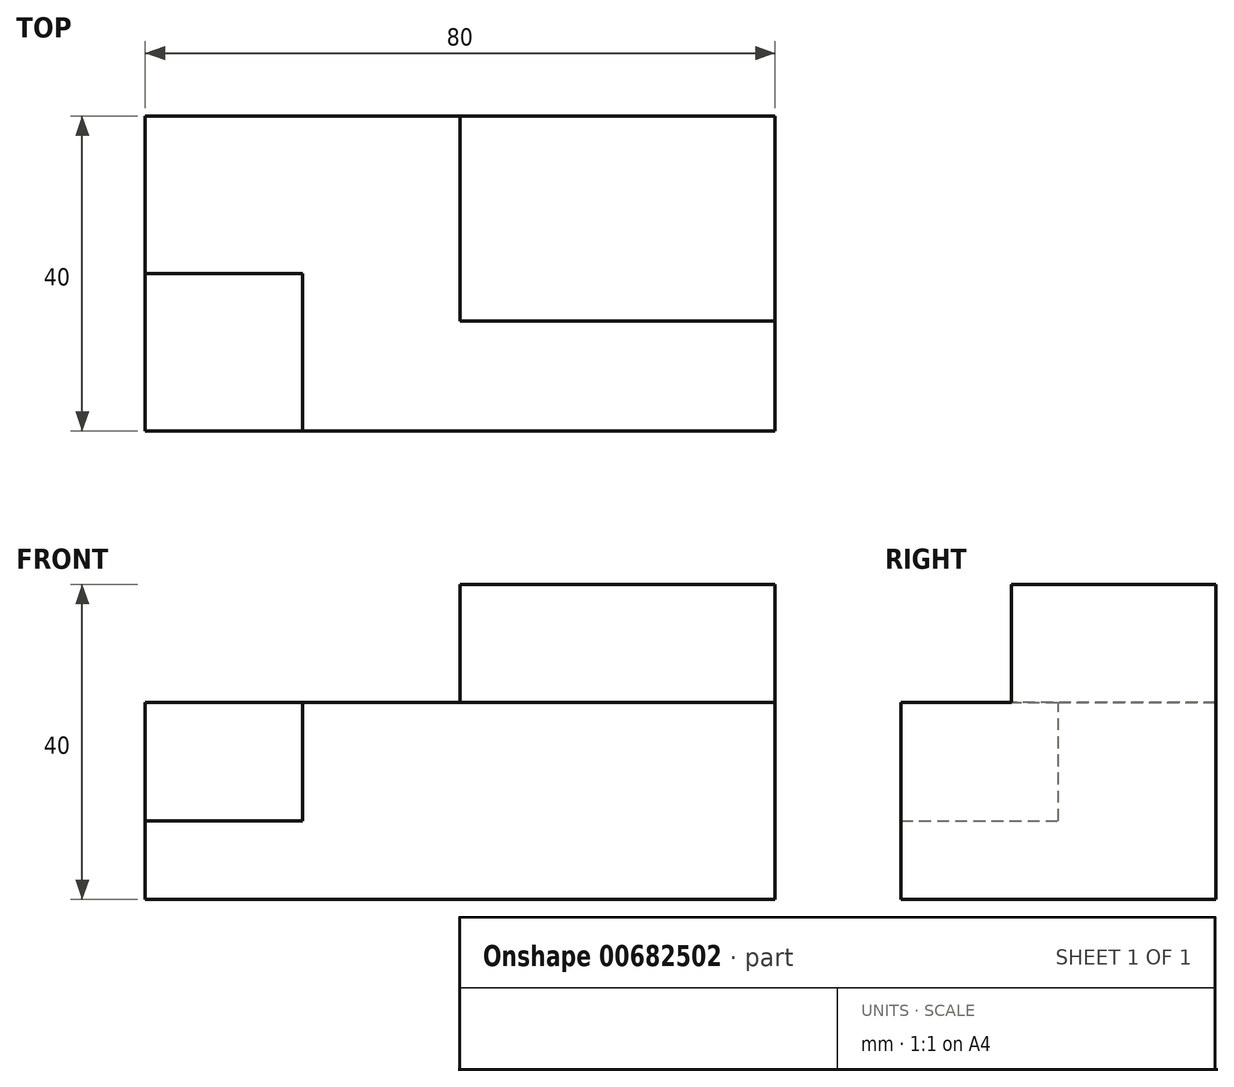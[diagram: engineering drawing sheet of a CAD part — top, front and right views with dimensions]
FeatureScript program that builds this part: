
annotation { "Feature Type Name" : "Feature", "Feature Type Description" : "" }
export const myFeature = defineFeature(function(context is Context, id is Id, definition is map)
    precondition{}
    {
        {
            var Q0;
            Q0=qCreatedBy(makeId("Top.planeOp"),FACE);
            var sketch = newSketch(context, id + "F0", { "sketchPlane" : qUnion([Q0])});
            skLineSegment(sketch, "E0.bottom", {"start": v(0, 0) * mm, "end": v(80, 0) * mm});
            skLineSegment(sketch, "E0.top", {"start": v(0, 40) * mm, "end": v(80, 40) * mm});
            skLineSegment(sketch, "E0.left", {"start": v(0, 0) * mm, "end": v(0, 40) * mm});
            skLineSegment(sketch, "E0.right", {"start": v(80, 0) * mm, "end": v(80, 40) * mm});
            skSolve(sketch);
        }
        {
            var Q0;
            Q0=makeQuery(id+"F0.imprint","IMPRINT",FACE,{"disambiguationData":[TD([[makeQuery(id+"F0.imprint","IMPRINT",EDGE,{"derivedFrom":sQuery(id+"F0.wireOp",EDGE,"E0.bottom")}),1.0]])]});
            extrude(context, id + "F1", {"entities" : qUnion([Q0]), "depth" : 25 * mm, "offsetDistance" : 25 * mm});
        }
        {
            var Q0;
            Q0=makeQuery(id+"F1.opExtrude","CAP_FACE",FACE,{"disambiguationData":[OSD([sQuery(id+"F0.wireOp",EDGE,"E0.bottom"),sQuery(id+"F0.wireOp",EDGE,"E0.top"),sQuery(id+"F0.wireOp",EDGE,"E0.left"),sQuery(id+"F0.wireOp",EDGE,"E0.right")])],"isStart":false});
            var sketch = newSketch(context, id + "F2", { "sketchPlane" : qUnion([Q0])});
            skLineSegment(sketch, "E1.bottom", {"start": v(80, 40) * mm, "end": v(40, 40) * mm});
            skLineSegment(sketch, "E1.top", {"start": v(80, 14) * mm, "end": v(40, 14) * mm});
            skLineSegment(sketch, "E1.left", {"start": v(80, 40) * mm, "end": v(80, 14) * mm});
            skLineSegment(sketch, "E1.right", {"start": v(40, 40) * mm, "end": v(40, 14) * mm});
            skSolve(sketch);
        }
        {
            var Q0;
            Q0=makeQuery(id+"F2.imprint","IMPRINT",FACE,{"disambiguationData":[TD([[makeQuery(id+"F2.imprint","IMPRINT",EDGE,{"derivedFrom":sQuery(id+"F2.wireOp",EDGE,"E1.bottom")}),-1.0]])]});
            extrude(context, id + "F3", {"entities" : qUnion([Q0]), "operationType" : NewBodyOperationType.ADD, "depth" : 15 * mm, "offsetDistance" : 25 * mm});
        }
        {
            var Q0;
            Q0=makeQuery(id+"F1.opExtrude","CAP_FACE",FACE,{"disambiguationData":[OSD([sQuery(id+"F0.wireOp",EDGE,"E0.bottom"),sQuery(id+"F0.wireOp",EDGE,"E0.top"),sQuery(id+"F0.wireOp",EDGE,"E0.left"),sQuery(id+"F0.wireOp",EDGE,"E0.right")])],"isStart":false});
            var sketch = newSketch(context, id + "F4", { "sketchPlane" : qUnion([Q0])});
            skPoint(sketch, "E2.oppositeSnap0", {"position": v(0, 20) * mm});
            skLineSegment(sketch, "E2.bottom", {"start": v(0, 0) * mm, "end": v(20, 0) * mm});
            skLineSegment(sketch, "E2.top", {"start": v(0, 20) * mm, "end": v(20, 20) * mm});
            skLineSegment(sketch, "E2.left", {"start": v(0, 0) * mm, "end": v(0, 20) * mm});
            skLineSegment(sketch, "E2.right", {"start": v(20, 0) * mm, "end": v(20, 20) * mm});
            skSolve(sketch);
        }
        {
            var Q0;
            Q0=makeQuery(id+"F4.imprint","IMPRINT",FACE,{"disambiguationData":[TD([[makeQuery(id+"F4.imprint","IMPRINT",EDGE,{"derivedFrom":sQuery(id+"F4.wireOp",EDGE,"E2.bottom")}),1.0]])]});
            extrude(context, id + "F5", {"entities" : qUnion([Q0]), "operationType" : NewBodyOperationType.REMOVE, "oppositeDirection" : true, "depth" : 15 * mm, "offsetDistance" : 25 * mm});
        }
    });
